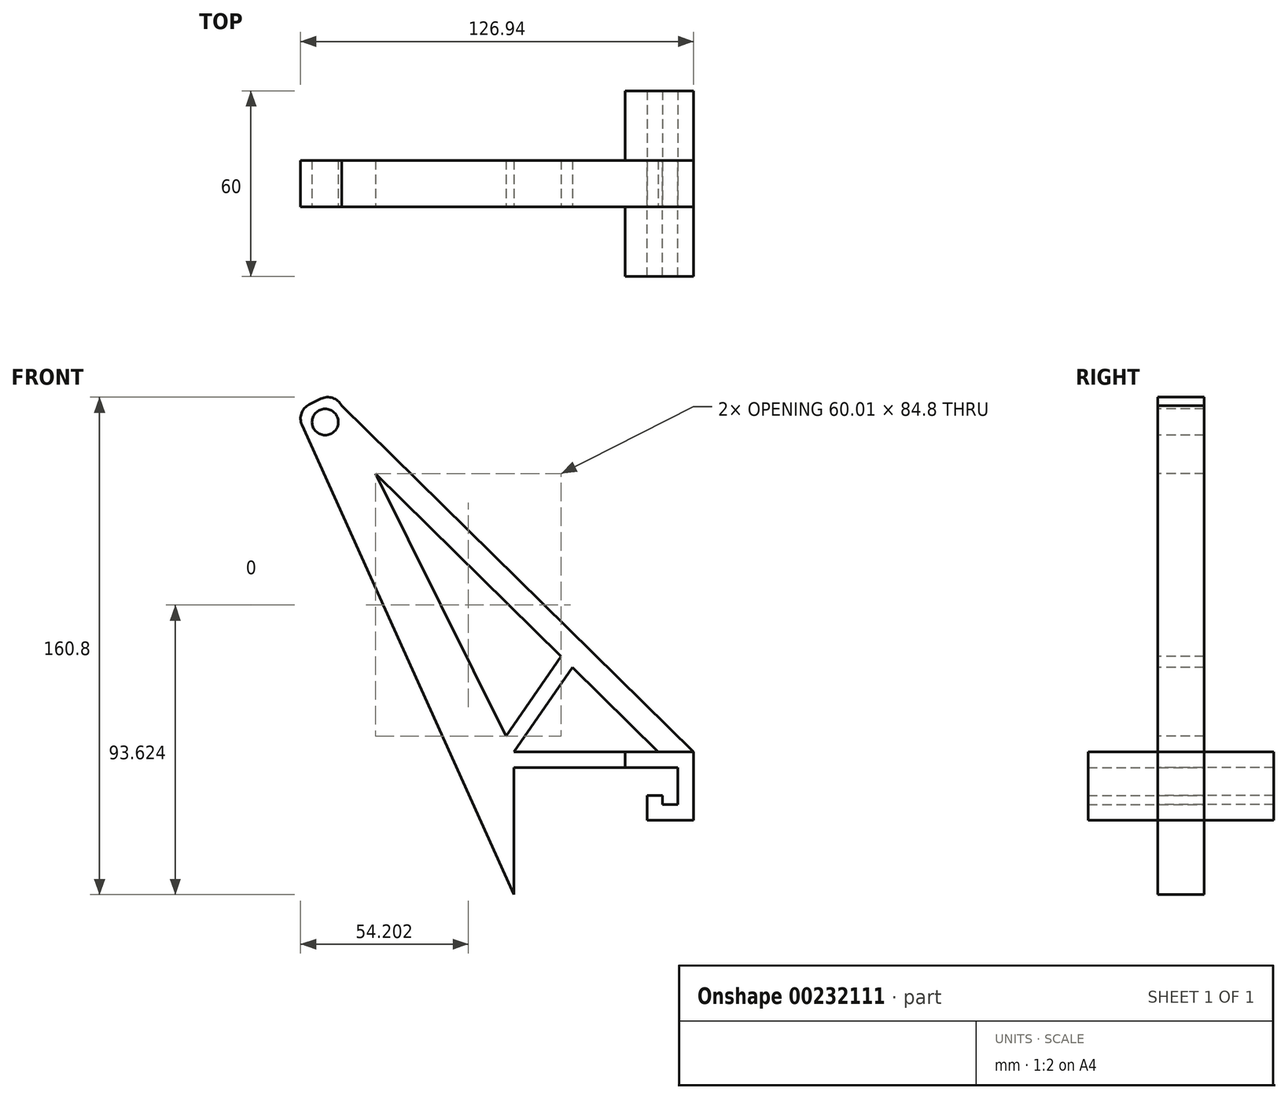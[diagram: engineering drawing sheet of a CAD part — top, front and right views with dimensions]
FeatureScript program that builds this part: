
annotation { "Feature Type Name" : "Feature", "Feature Type Description" : "" }
export const myFeature = defineFeature(function(context is Context, id is Id, definition is map)
    precondition{}
    {
        {
            var Q0;
            Q0=qCreatedBy(makeId("Front.planeOp"),FACE);
            var sketch = newSketch(context, id + "F0", { "sketchPlane" : qUnion([Q0])});
            skLineSegment(sketch, "E0", {"start": v(9.24, -83.63) * mm, "end": v(62.24, -83.63) * mm});
            skLineSegment(sketch, "E1", {"start": v(62.24, -83.63) * mm, "end": v(62.24, -95.63) * mm});
            skLineSegment(sketch, "E2", {"start": v(62.24, -95.63) * mm, "end": v(57.24, -95.63) * mm});
            skLineSegment(sketch, "E3", {"start": v(57.24, -95.63) * mm, "end": v(57.24, -92.63) * mm});
            skLineSegment(sketch, "E4", {"start": v(57.24, -92.63) * mm, "end": v(52.24, -92.63) * mm});
            skLineSegment(sketch, "E5", {"start": v(52.24, -92.63) * mm, "end": v(52.24, -100.63) * mm});
            skLineSegment(sketch, "E6", {"start": v(52.24, -100.63) * mm, "end": v(67.24, -100.63) * mm});
            skLineSegment(sketch, "E7", {"start": v(67.24, -100.63) * mm, "end": v(67.24, -78.63) * mm});
            skLineSegment(sketch, "E8", {"start": v(67.24, -78.63) * mm, "end": v(9.24, -78.63) * mm});
            skLineSegment(sketch, "E9", {"start": v(9.24, -78.63) * mm, "end": v(-46.45, 33.29) * mm});
            skLineSegment(sketch, "E10", {"start": v(-53.15, 35.54) * mm, "end": v(-56.93, 33.66) * mm});
            skLineSegment(sketch, "E11", {"start": v(-59.26, 27.12) * mm, "end": v(9.24, -124.74) * mm});
            skLineSegment(sketch, "E12", {"start": v(9.24, -124.74) * mm, "end": v(9.24, -83.63) * mm});
            skPoint(sketch, "E13.visualSharp", {"position": v(-48.68, 37.76) * mm});
            skArc(sketch, "E13.filletArc", {"start": v(-46.45, 33.29) * mm, "mid": v(-49.34, 35.8) * mm, "end": v(-53.15, 35.54) * mm});
            skPoint(sketch, "E14.visualSharp", {"position": v(-61.24, 31.51) * mm});
            skArc(sketch, "E14.filletArc", {"start": v(-56.93, 33.66) * mm, "mid": v(-59.41, 30.86) * mm, "end": v(-59.26, 27.12) * mm});
            skCircle(sketch, "E15", {"center": v(-51.77, 28.02) * mm, "radius": 4.25 * mm});
            skLineSegment(sketch, "E16", {"start": v(-46.45, 33.29) * mm, "end": v(67.24, -78.63) * mm});
            skLineSegment(sketch, "E17", {"start": v(-35.5, 11.28) * mm, "end": v(55.83, -78.63) * mm});
            skLineSegment(sketch, "E18", {"start": v(9.24, -78.63) * mm, "end": v(28.12, -51.35) * mm});
            skLineSegment(sketch, "E19", {"start": v(28.12, -51.35) * mm, "end": v(24.5, -47.79) * mm});
            skLineSegment(sketch, "E20", {"start": v(24.5, -47.79) * mm, "end": v(6.7, -73.51) * mm});
            skLineSegment(sketch, "E21", {"start": v(45.12, -83.63) * mm, "end": v(45.12, -78.63) * mm});
            skSolve(sketch);
        }
        {
            var Q0;
            Q0=makeQuery(id+"F0.imprint","IMPRINT",FACE,{"disambiguationData":[TD([[makeQuery(id+"F0.imprint","IMPRINT",EDGE,{"derivedFrom":sQuery(id+"F0.wireOp",EDGE,"E0")}),1.0]])]});
            var Q1;
            {var subQ4=sQuery(id+"F0.wireOp",EDGE,"E16");Q1=makeQuery(id+"F0.imprint","IMPRINT",FACE,{"disambiguationData":[TD([[makeQuery(id+"F0.imprint","IMPRINT",EDGE,{"derivedFrom":subQ4}),-1.0]])]});}
            var Q2;
            {var subQ0=sQuery(id+"F0.wireOp",EDGE,"E18");Q2=makeQuery(id+"F0.imprint","IMPRINT",FACE,{"disambiguationData":[TD([[makeQuery(id+"F0.imprint","IMPRINT",EDGE,{"derivedFrom":subQ0}),1.0]])]});}
            extrude(context, id + "F1", {"entities" : qUnion([Q0, Q1, Q2]), "endBound" : BoundingType.SYMMETRIC, "depth" : 15 * mm});
        }
        {
            var Q0;
            {var subQ1=sQuery(id+"F0.wireOp",EDGE,"E1");Q0=makeQuery(id+"F0.imprint","IMPRINT",FACE,{"disambiguationData":[TD([[makeQuery(id+"F0.imprint","IMPRINT",EDGE,{"derivedFrom":subQ1}),1.0]])]});}
            var Q1;
            Q1=makeQuery(id+"F0.imprint","IMPRINT",FACE,{"disambiguationData":[TD([[makeQuery(id+"F0.imprint","IMPRINT",EDGE,{"derivedFrom":sQuery(id+"F0.wireOp",EDGE,"E10")}),1.0]])]});
            extrude(context, id + "F2", {"entities" : qUnion([Q0, Q1]), "operationType" : NewBodyOperationType.ADD, "endBound" : BoundingType.SYMMETRIC, "depth" : 15 * mm});
        }
        {
            var Q0;
            {var subQ1=sQuery(id+"F0.wireOp",EDGE,"E1");Q0=makeQuery(id+"F0.imprint","IMPRINT",FACE,{"disambiguationData":[TD([[makeQuery(id+"F0.imprint","IMPRINT",EDGE,{"derivedFrom":subQ1}),1.0]])]});}
            extrude(context, id + "F3", {"entities" : qUnion([Q0]), "operationType" : NewBodyOperationType.ADD, "depth" : 30 * mm});
        }
        {
            var Q0;
            Q0=makeQuery(id+"F1.opExtrude","SWEPT_BODY",BODY,{"disambiguationData":[OSD([sQuery(id+"F0.wireOp",EDGE,"E0"),sQuery(id+"F0.wireOp",EDGE,"E1"),sQuery(id+"F0.wireOp",EDGE,"E2"),sQuery(id+"F0.wireOp",EDGE,"E3"),sQuery(id+"F0.wireOp",EDGE,"E4"),sQuery(id+"F0.wireOp",EDGE,"E5"),sQuery(id+"F0.wireOp",EDGE,"E6"),sQuery(id+"F0.wireOp",EDGE,"E7"),sQuery(id+"F0.wireOp",EDGE,"E8"),sQuery(id+"F0.wireOp",EDGE,"E9"),sQuery(id+"F0.wireOp",EDGE,"E16"),sQuery(id+"F0.wireOp",EDGE,"E17"),sQuery(id+"F0.wireOp",EDGE,"E18"),sQuery(id+"F0.wireOp",EDGE,"E20"),sQuery(id+"F0.wireOp",EDGE,"E21")])]});
            var Q1;
            Q1=qCreatedBy(makeId("Front.planeOp"),FACE);
            mirror(context, id + "F4", {"entities" : qUnion([Q0]), "mirrorPlane" : qUnion([Q1])});
        }
    });
